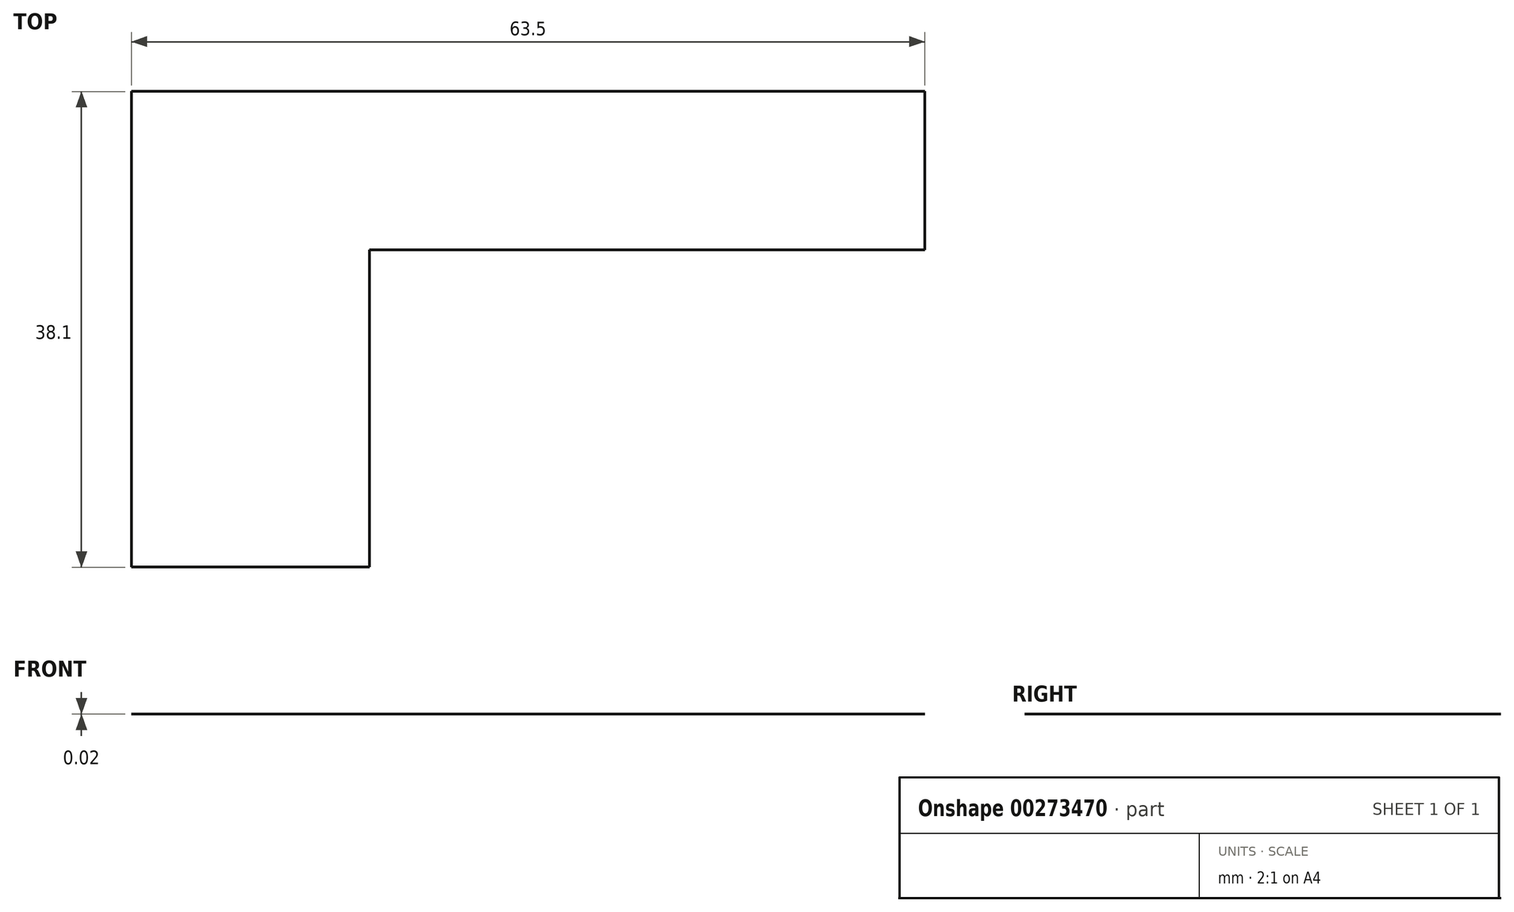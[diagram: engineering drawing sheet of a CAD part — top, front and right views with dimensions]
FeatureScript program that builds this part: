
annotation { "Feature Type Name" : "Feature", "Feature Type Description" : "" }
export const myFeature = defineFeature(function(context is Context, id is Id, definition is map)
    precondition{}
    {
        {
            var Q0;
            Q0=qCreatedBy(makeId("Top.planeOp"),FACE);
            var sketch = newSketch(context, id + "F0", { "sketchPlane" : qUnion([Q0])});
            skLineSegment(sketch, "E0", {"start": v(-45.85, -13.56) * mm, "end": v(-45.85, 24.54) * mm});
            skLineSegment(sketch, "E1", {"start": v(-45.85, 24.54) * mm, "end": v(17.65, 24.54) * mm});
            skLineSegment(sketch, "E2", {"start": v(17.65, 24.54) * mm, "end": v(17.65, 11.84) * mm});
            skLineSegment(sketch, "E3", {"start": v(17.65, 11.84) * mm, "end": v(-26.8, 11.84) * mm});
            skLineSegment(sketch, "E4", {"start": v(-26.8, 11.84) * mm, "end": v(-26.8, -13.56) * mm});
            skLineSegment(sketch, "E5", {"start": v(-26.8, -13.56) * mm, "end": v(-45.85, -13.56) * mm});
            skSolve(sketch);
        }
        {
            var Q0;
            Q0=makeQuery(id+"F0.imprint","IMPRINT",FACE,{"disambiguationData":[TD([[makeQuery(id+"F0.imprint","IMPRINT",EDGE,{"derivedFrom":sQuery(id+"F0.wireOp",EDGE,"E0")}),-1.0]])]});
            extrude(context, id + "F1", {"entities" : qUnion([Q0]), "depth" : 1 / 50.8 * mm});
        }
    });
